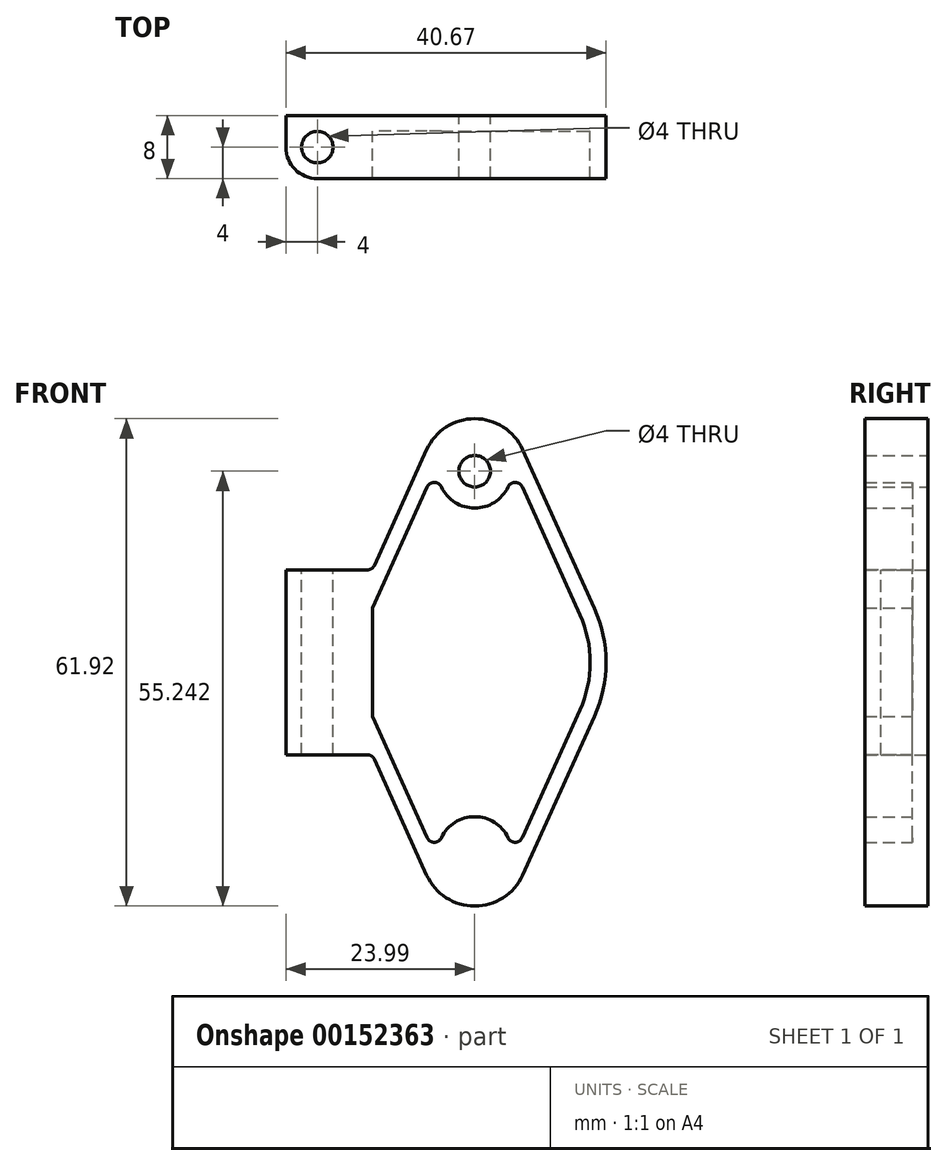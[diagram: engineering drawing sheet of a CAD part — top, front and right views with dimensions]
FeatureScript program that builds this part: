
annotation { "Feature Type Name" : "Feature", "Feature Type Description" : "" }
export const myFeature = defineFeature(function(context is Context, id is Id, definition is map)
    precondition{}
    {
        {
            var Q0;
            Q0=qCreatedBy(makeId("Front.planeOp"),FACE);
            var sketch = newSketch(context, id + "F0", { "sketchPlane" : qUnion([Q0])});
            skArc(sketch, "E0", {"start": v(6.09, 27.03) * mm, "mid": v(0, 30.96) * mm, "end": v(-6.09, 27.03) * mm});
            skArc(sketch, "E1.MirrorC", {"start": v(6.09, -27.03) * mm, "mid": v(0, -30.96) * mm, "end": v(-6.09, -27.03) * mm});
            skArc(sketch, "E2", {"start": v(-15.2, 6.86) * mm, "mid": v(-16.68, 0) * mm, "end": v(-15.2, -6.86) * mm, "construction": true});
            skLineSegment(sketch, "E3", {"start": v(-6.09, 27.03) * mm, "end": v(-15.2, 6.86) * mm});
            skLineSegment(sketch, "E4.MirrorCS", {"start": v(-6.09, -27.03) * mm, "end": v(-15.2, -6.86) * mm});
            skLineSegment(sketch, "E5.MirrorCS", {"start": v(6.09, 27.03) * mm, "end": v(15.2, 6.86) * mm});
            skLineSegment(sketch, "E6.MirrorCS", {"start": v(6.09, -27.03) * mm, "end": v(15.2, -6.86) * mm});
            skArc(sketch, "E7.trimOffspring", {"start": v(15.2, -6.86) * mm, "mid": v(16.68, 0) * mm, "end": v(15.2, 6.86) * mm});
            skCircle(sketch, "E8", {"center": v(0, 24.28) * mm, "radius": 2 * mm});
            skCircle(sketch, "E9.MirrorC", {"center": v(0, -24.28) * mm, "radius": 2 * mm});
            skLineSegment(sketch, "E10.1", {"start": v(-6.05, 22.27) * mm, "end": v(-13.37, 6.04) * mm});
            skLineSegment(sketch, "E10.2", {"start": v(6.05, 22.27) * mm, "end": v(13.37, 6.04) * mm});
            skArc(sketch, "E10.3", {"start": v(-13.37, 6.04) * mm, "mid": v(-14.68, 0) * mm, "end": v(-13.37, -6.04) * mm, "construction": true});
            skArc(sketch, "E10.4", {"start": v(13.37, -6.04) * mm, "mid": v(14.68, 0) * mm, "end": v(13.37, 6.04) * mm});
            skLineSegment(sketch, "E10.5", {"start": v(6.05, -22.27) * mm, "end": v(13.37, -6.04) * mm});
            skLineSegment(sketch, "E10.7", {"start": v(-6.05, -22.27) * mm, "end": v(-13.37, -6.04) * mm});
            skArc(sketch, "E11", {"start": v(-4.23, 22.28) * mm, "mid": v(0, 19.6) * mm, "end": v(4.23, 22.28) * mm});
            skArc(sketch, "E12", {"start": v(4.23, -22.28) * mm, "mid": v(0, -19.6) * mm, "end": v(-4.23, -22.28) * mm});
            skPoint(sketch, "E13.visualSharp", {"position": v(-4.27, 26.2) * mm});
            skArc(sketch, "E13.filletArc", {"start": v(-4.23, 22.28) * mm, "mid": v(-5.14, 22.85) * mm, "end": v(-6.05, 22.27) * mm});
            skPoint(sketch, "E14.visualSharp", {"position": v(4.27, 26.2) * mm});
            skArc(sketch, "E14.filletArc", {"start": v(6.05, 22.27) * mm, "mid": v(5.14, 22.85) * mm, "end": v(4.23, 22.28) * mm});
            skPoint(sketch, "E15.visualSharp", {"position": v(4.27, -26.2) * mm});
            skArc(sketch, "E15.filletArc", {"start": v(4.23, -22.28) * mm, "mid": v(5.14, -22.85) * mm, "end": v(6.05, -22.27) * mm});
            skPoint(sketch, "E16.visualSharp", {"position": v(-4.27, -26.2) * mm});
            skArc(sketch, "E16.filletArc", {"start": v(-6.05, -22.27) * mm, "mid": v(-5.14, -22.85) * mm, "end": v(-4.23, -22.28) * mm});
            skLineSegment(sketch, "E17", {"start": v(-24, 11.75) * mm, "end": v(-13, 11.75) * mm});
            skLineSegment(sketch, "E18.MirrorCS", {"start": v(-24, -11.75) * mm, "end": v(-13, -11.75) * mm});
            skLineSegment(sketch, "E19", {"start": v(-24, 11.75) * mm, "end": v(-24, -11.75) * mm});
            skLineSegment(sketch, "E20", {"start": v(-13, 11.75) * mm, "end": v(-13, -11.75) * mm});
            skSolve(sketch);
        }
        {
            var Q0;
            Q0=makeQuery(id+"F0.imprint","IMPRINT",FACE,{"disambiguationData":[TD([[makeQuery(id+"F0.imprint","IMPRINT",EDGE,{"derivedFrom":sQuery(id+"F0.wireOp",EDGE,"E0")}),1.0]])]});
            var Q1;
            Q1=makeQuery(id+"F0.imprint","IMPRINT",FACE,{"disambiguationData":[TD([[makeQuery(id+"F0.imprint","IMPRINT",EDGE,{"derivedFrom":sQuery(id+"F0.wireOp",EDGE,"3e905b6d-8bee-4998-9225-6dcc00ec54d6.0")}),1.0]])]});
            var Q2;
            {var subQ0=sQuery(id+"F0.wireOp",EDGE,"V3VQVJa9-jFdV-kq6X-8dhK-Xa6uhI9IwXRv");Q2=makeQuery(id+"F0.imprint","IMPRINT",FACE,{"disambiguationData":[TD([[makeQuery(id+"F0.imprint","IMPRINT",EDGE,{"derivedFrom":subQ0}),1.0]])]});}
            var Q3;
            {var subQ0=sQuery(id+"F0.wireOp",EDGE,"fO4OrWz9-9ff7-9GLH-ZSri-iVDJwJIuYxIB");Q3=makeQuery(id+"F0.imprint","IMPRINT",FACE,{"disambiguationData":[TD([[makeQuery(id+"F0.imprint","IMPRINT",EDGE,{"derivedFrom":subQ0}),1.0]])]});}
            var Q4;
            Q4=makeQuery(id+"F0.imprint","IMPRINT",FACE,{"disambiguationData":[TD([[makeQuery(id+"F0.imprint","IMPRINT",EDGE,{"derivedFrom":sQuery(id+"F0.wireOp",EDGE,"E9.MirrorC")}),1.0]])]});
            var Q5;
            Q5=makeQuery(id+"F0.imprint","IMPRINT",FACE,{"disambiguationData":[TD([[makeQuery(id+"F0.imprint","IMPRINT",EDGE,{"derivedFrom":sQuery(id+"F0.wireOp",EDGE,"E8")}),-1.0]])]});
            var Q6;
            {var subQ1=sQuery(id+"F0.wireOp",EDGE,"E17");Q6=makeQuery(id+"F0.imprint","IMPRINT",FACE,{"disambiguationData":[TD([[makeQuery(id+"F0.imprint","IMPRINT",EDGE,{"derivedFrom":subQ1}),-1.0]])]});}
            extrude(context, id + "F1", {"entities" : qUnion([Q0, Q1, Q2, Q3, Q4, Q5, Q6]), "depth" : 8 * mm});
        }
        {
            var Q0;
            {var subQ2=sQuery(id+"F0.wireOp",EDGE,"E10.1");Q0=makeQuery(id+"F0.imprint","IMPRINT",FACE,{"disambiguationData":[TD([[makeQuery(id+"F0.imprint","IMPRINT",EDGE,{"derivedFrom":subQ2}),1.0]])]});}
            var Q1;
            {var subQ1=sQuery(id+"F0.wireOp",EDGE,"E1.MirrorC");Q1=makeQuery(id+"F0.imprint","IMPRINT",FACE,{"disambiguationData":[TD([[makeQuery(id+"F0.imprint","IMPRINT",EDGE,{"derivedFrom":subQ1}),1.0]])]});}
            var Q2;
            {var subQ1=sQuery(id+"F0.wireOp",EDGE,"E2");Q2=makeQuery(id+"F0.imprint","IMPRINT",FACE,{"disambiguationData":[TD([[makeQuery(id+"F0.imprint","IMPRINT",EDGE,{"derivedFrom":subQ1}),-1.0]])]});}
            extrude(context, id + "F2", {"entities" : qUnion([Q0, Q1, Q2]), "operationType" : NewBodyOperationType.ADD, "depth" : 2 * mm});
        }
        {
            var Q0;
            Q0=makeQuery(id+"F1.opExtrude","SWEPT_EDGE",EDGE,{"disambiguationData":[OSD([sQuery(id+"F0.wireOp",EDGE,"E4.MirrorCS"),sQuery(id+"F0.wireOp",EDGE,"4593fb65-0ce5-46c1-99e0-68ac4d03a7a10.MirrorCS")])]});
            var Q1;
            Q1=makeQuery(id+"F1.opExtrude","SWEPT_EDGE",EDGE,{"disambiguationData":[OSD([sQuery(id+"F0.wireOp",EDGE,"E4.MirrorCS"),sQuery(id+"F0.wireOp",EDGE,"E18.MirrorCS")])]});
            var Q2;
            Q2=makeQuery(id+"F1.opExtrude","SWEPT_EDGE",EDGE,{"disambiguationData":[OSD([sQuery(id+"F0.wireOp",EDGE,"E3"),sQuery(id+"F0.wireOp",EDGE,"aPWfCUQh-ARNy-KCd3-gmNS-Fh44m6qCemxU")])]});
            var Q3;
            Q3=makeQuery(id+"F1.opExtrude","SWEPT_EDGE",EDGE,{"disambiguationData":[OSD([sQuery(id+"F0.wireOp",EDGE,"E3"),sQuery(id+"F0.wireOp",EDGE,"E17")])]});
            fillet(context, id + "F3", {"entities" : qUnion([Q0, Q1, Q2, Q3]), "radius" : 1 * mm, "tangentPropagation" : true, "allowEdgeOverflow" : false});
        }
        {
            var Q0;
            Q0=makeQuery(id+"F1.opExtrude","SWEPT_FACE",FACE,{"disambiguationData":[OSD([sQuery(id+"F0.wireOp",EDGE,"E17")])]});
            var sketch = newSketch(context, id + "F4", { "sketchPlane" : qUnion([Q0])});
            skPoint(sketch, "E21", {"position": v(-20, -4) * mm});
            skLineSegment(sketch, "E22", {"start": v(-24, 0) * mm, "end": v(-20, -4) * mm, "construction": true});
            skLineSegment(sketch, "E23", {"start": v(-20, -4) * mm, "end": v(-24, -8) * mm, "construction": true});
            skSolve(sketch);
        }
        {
            var Q0;
            Q0=sQuery(id+"F4.wireOp",VERTEX,"E21");
            var Q1;
            Q1=makeQuery(id+"F1.opExtrude","SWEPT_BODY",BODY,{"disambiguationData":[OSD([sQuery(id+"F0.wireOp",EDGE,"E0"),sQuery(id+"F0.wireOp",EDGE,"E2"),sQuery(id+"F0.wireOp",EDGE,"E3"),sQuery(id+"F0.wireOp",EDGE,"E5.MirrorCS"),sQuery(id+"F0.wireOp",EDGE,"E7.trimOffspring"),sQuery(id+"F0.wireOp",EDGE,"S2IiUO7s-7rjS-UU1n-G3Er-isHJvikYOna3"),sQuery(id+"F0.wireOp",EDGE,"U4xu2M48-wPnJ-tMoa-V4Px-PJSouQ81H8F5"),sQuery(id+"F0.wireOp",EDGE,"HV652KFt-d8Xn-WSbo-tHCJ-cfUj0g3Xd7DK"),sQuery(id+"F0.wireOp",EDGE,"fO4OrWz9-9ff7-9GLH-ZSri-iVDJwJIuYxIB"),sQuery(id+"F0.wireOp",EDGE,"zmEnNPUg-k7De-l4Ih-Irfg-M27UcczaaJBl"),sQuery(id+"F0.wireOp",EDGE,"V3VQVJa9-jFdV-kq6X-8dhK-Xa6uhI9IwXRv"),sQuery(id+"F0.wireOp",EDGE,"W1IEodJy-6PRz-xiH1-2iNf-kAuRcIV7mYlj"),sQuery(id+"F0.wireOp",EDGE,"5ZKJKvnk-ET5z-qlB3-oLW5-LuLVHKlnV0HX"),sQuery(id+"F0.wireOp",EDGE,"Gk8awqwg-zgXA-VnUW-8MKI-QdblR6Wf13JX"),sQuery(id+"F0.wireOp",EDGE,"WIDdAYBM-okhh-eBsl-QBhJ-HuDdJqstO0Cl"),sQuery(id+"F0.wireOp",EDGE,"iXw4nrh7-EQqi-IiG2-VBaK-kNldmVsmUaTg"),sQuery(id+"F0.wireOp",EDGE,"03ff63bc-461f-42e4-a166-82e271801758"),sQuery(id+"F0.wireOp",EDGE,"5881da14-4dba-48e3-8e12-341ecdeeb7140.MirrorCS")])]});
            hole(context, id + "F5", {"style" : HoleStyle.SIMPLE, "endStyle" : HoleEndStyle.THROUGH, "standardTappedOrClearance" : lookupTablePath({ "standard" : "ISO", "size" : "4", "type" : "Drilled" }), "standardBlindInLast" : lookupTablePath({ "standard" : "ISO", "size" : "4", "type" : "Drilled" }), "holeDiameter" : 4 * mm, "locations" : qUnion([Q0]), "scope" : qUnion([Q1]), "isTappedThrough" : true});
        }
        {
            var Q0;
            Q0=makeQuery(id+"F1.opExtrude","CAP_EDGE",EDGE,{"disambiguationData":[OSD([sQuery(id+"F0.wireOp",EDGE,"E19")])],"isStart":false});
            fillet(context, id + "F6", {"entities" : qUnion([Q0]), "radius" : (8 / 2) * mm, "tangentPropagation" : true, "allowEdgeOverflow" : false});
        }
    });
